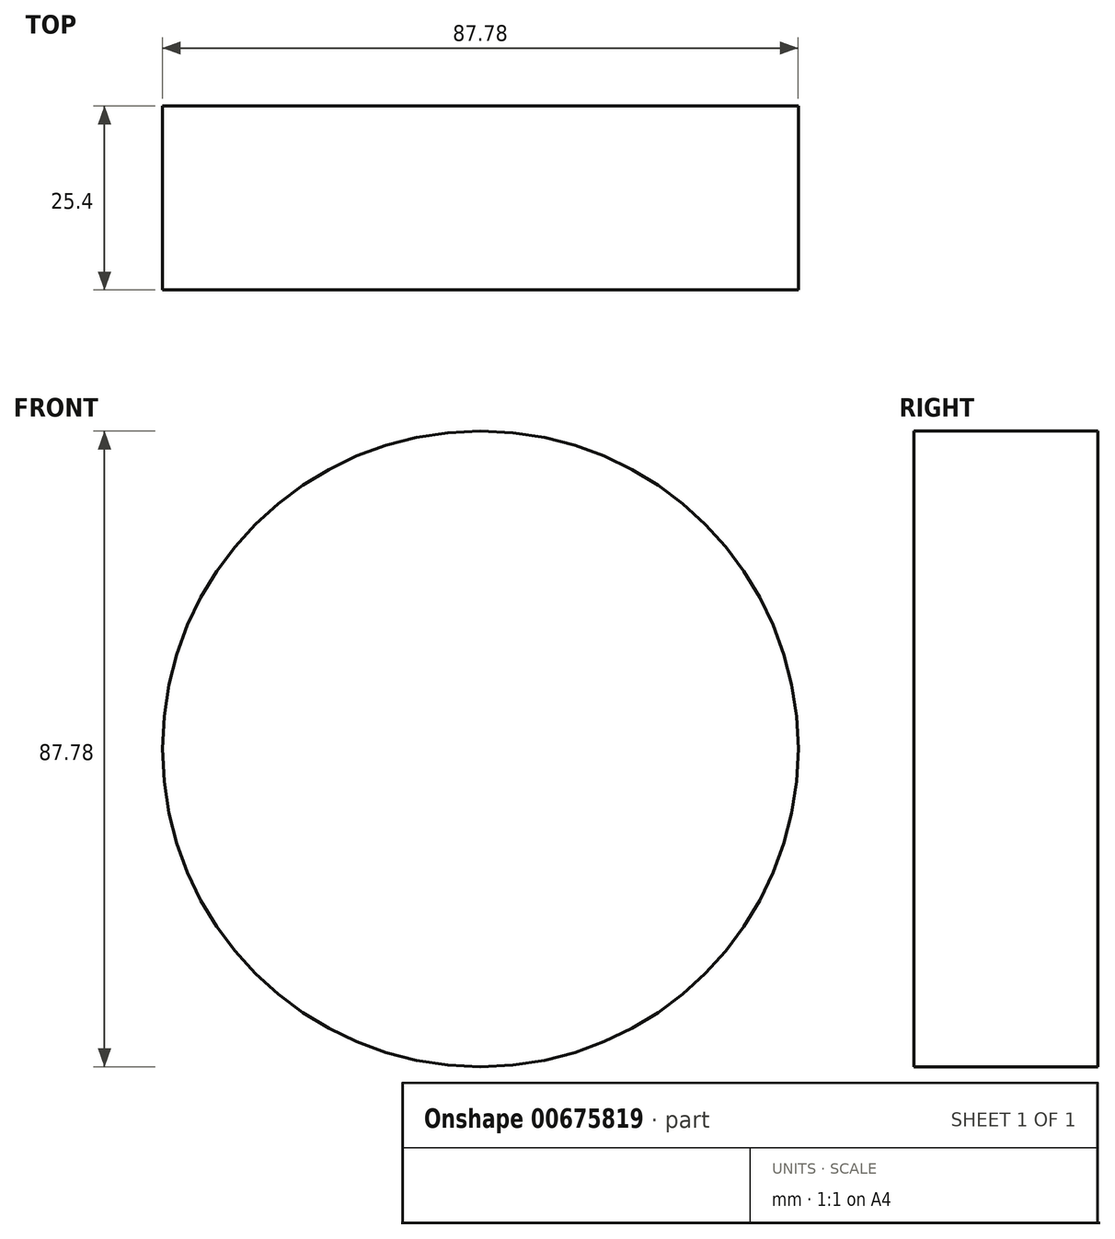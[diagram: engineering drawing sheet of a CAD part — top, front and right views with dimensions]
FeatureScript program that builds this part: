
annotation { "Feature Type Name" : "Feature", "Feature Type Description" : "" }
export const myFeature = defineFeature(function(context is Context, id is Id, definition is map)
    precondition{}
    {
        {
            var Q0;
            Q0=qCreatedBy(makeId("Front.planeOp"),FACE);
            var sketch = newSketch(context, id + "F0", { "sketchPlane" : qUnion([Q0])});
            skCircle(sketch, "E0", {"center": v(0, 3.65) * mm, "radius": 43.9 * mm});
            skSolve(sketch);
        }
        {
            var Q0;
            Q0=makeQuery(id+"F0.imprint","IMPRINT",FACE,{"disambiguationData":[TD([[makeQuery(id+"F0.imprint","IMPRINT",EDGE,{"derivedFrom":sQuery(id+"F0.wireOp",EDGE,"E0")}),1.0]])]});
            extrude(context, id + "F1", {"entities" : qUnion([Q0]), "depth" : 25.4 * mm, "offsetDistance" : 25.4 * mm});
        }
    });
